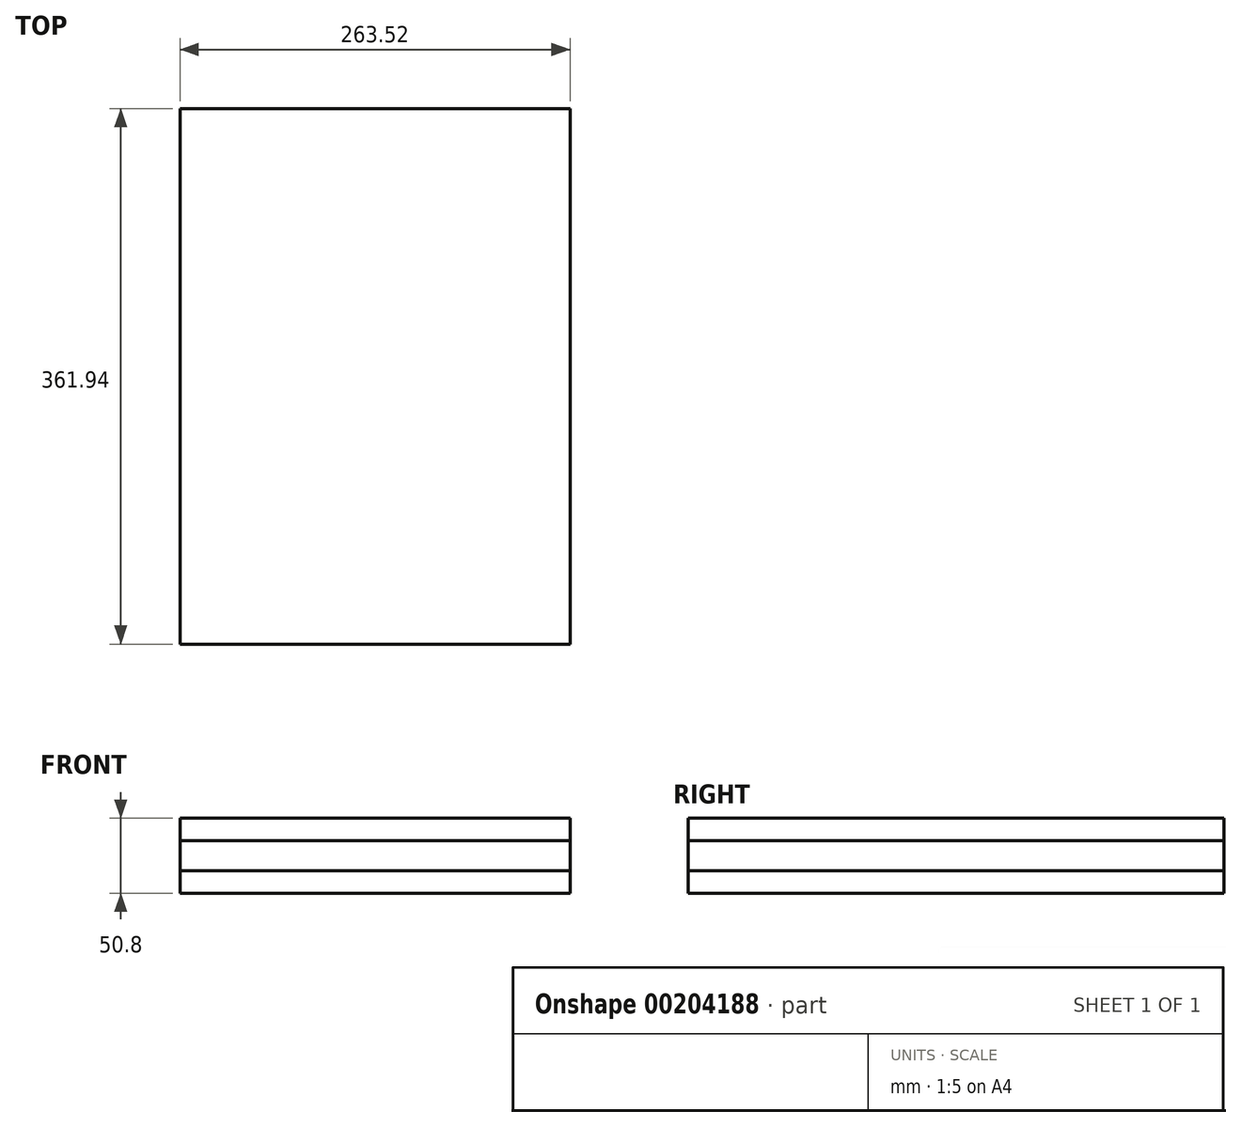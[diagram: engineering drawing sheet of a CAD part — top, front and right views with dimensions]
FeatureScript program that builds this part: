
annotation { "Feature Type Name" : "Feature", "Feature Type Description" : "" }
export const myFeature = defineFeature(function(context is Context, id is Id, definition is map)
    precondition{}
    {
        {
            var Q0;
            Q0=qCreatedBy(makeId("Top.planeOp"),FACE);
            var sketch = newSketch(context, id + "F0", { "sketchPlane" : qUnion([Q0])});
            skLineSegment(sketch, "E0.bottom", {"start": v(131.76, 180.98) * mm, "end": v(-131.76, 180.98) * mm});
            skLineSegment(sketch, "E0.top", {"start": v(131.76, -180.98) * mm, "end": v(-131.76, -180.98) * mm});
            skLineSegment(sketch, "E0.left", {"start": v(131.76, 180.98) * mm, "end": v(131.76, -180.98) * mm});
            skLineSegment(sketch, "E0.right", {"start": v(-131.76, 180.98) * mm, "end": v(-131.76, -180.98) * mm});
            skPoint(sketch, "E0.middle", {"position": v(0, 0) * mm});
            skSolve(sketch);
        }
        {
            var Q0;
            Q0=makeQuery(id+"F0.imprint","IMPRINT",FACE,{"disambiguationData":[TD([[makeQuery(id+"F0.imprint","IMPRINT",EDGE,{"derivedFrom":sQuery(id+"F0.wireOp",EDGE,"E0.bottom")}),1.0]])]});
            extrude(context, id + "F1", {"entities" : qUnion([Q0]), "depth" : 10.16 * mm, "hasSecondDirection" : true, "secondDirectionOppositeDirection" : true, "secondDirectionDepth" : 10.16 * mm});
        }
        {
            var Q0;
            Q0 = qSketchRegion(id + "F0", true);
            extrude(context, id + "F2", {"entities" : qUnion([Q0]), "depth" : 25.4 * mm, "hasSecondDirection" : true, "secondDirectionOppositeDirection" : true, "secondDirectionDepth" : 25.4 * mm});
        }
    });
